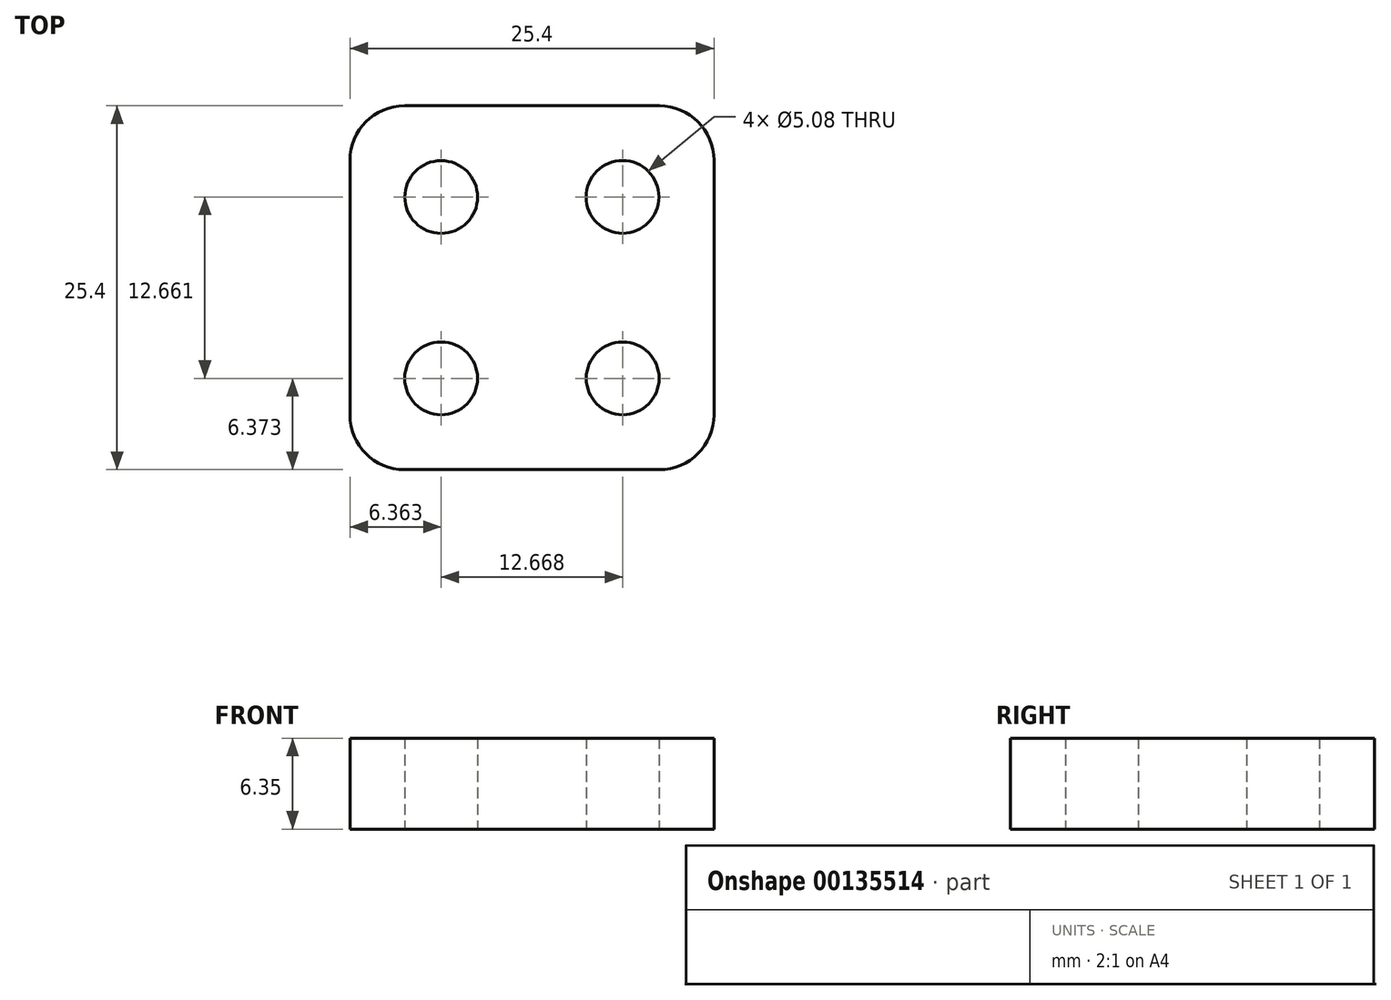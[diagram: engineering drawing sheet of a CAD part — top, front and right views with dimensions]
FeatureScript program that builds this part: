
annotation { "Feature Type Name" : "Feature", "Feature Type Description" : "" }
export const myFeature = defineFeature(function(context is Context, id is Id, definition is map)
    precondition{}
    {
        {
            var Q0;
            Q0=qCreatedBy(makeId("Top.planeOp"),FACE);
            var sketch = newSketch(context, id + "F0", { "sketchPlane" : qUnion([Q0])});
            skLineSegment(sketch, "E0.bottom", {"start": v(8.9, -12.7) * mm, "end": v(-8.9, -12.7) * mm});
            skLineSegment(sketch, "E0.top", {"start": v(8.9, 12.7) * mm, "end": v(-8.9, 12.7) * mm});
            skLineSegment(sketch, "E0.left", {"start": v(12.7, -8.9) * mm, "end": v(12.7, 8.9) * mm});
            skLineSegment(sketch, "E0.right", {"start": v(-12.7, -8.9) * mm, "end": v(-12.7, 8.9) * mm});
            skPoint(sketch, "E0.middle", {"position": v(0, 0) * mm});
            skPoint(sketch, "E1.visualSharp", {"position": v(-12.7, -12.7) * mm});
            skArc(sketch, "E1.filletArc", {"start": v(-12.7, -8.9) * mm, "mid": v(-11.58, -11.58) * mm, "end": v(-8.9, -12.7) * mm});
            skPoint(sketch, "E2.visualSharp", {"position": v(12.7, -12.7) * mm});
            skArc(sketch, "E2.filletArc", {"start": v(8.9, -12.7) * mm, "mid": v(11.58, -11.58) * mm, "end": v(12.7, -8.9) * mm});
            skPoint(sketch, "E3.visualSharp", {"position": v(-12.7, 12.7) * mm});
            skArc(sketch, "E3.filletArc", {"start": v(-8.9, 12.7) * mm, "mid": v(-11.58, 11.58) * mm, "end": v(-12.7, 8.9) * mm});
            skPoint(sketch, "E4.visualSharp", {"position": v(12.7, 12.7) * mm});
            skArc(sketch, "E4.filletArc", {"start": v(12.7, 8.9) * mm, "mid": v(11.58, 11.58) * mm, "end": v(8.9, 12.7) * mm});
            skSolve(sketch);
        }
        {
            var Q0;
            Q0 = qSketchRegion(id + "F0", true);
            extrude(context, id + "F1", {"entities" : qUnion([Q0]), "depth" : 6.35 * mm});
        }
        {
            var Q0;
            Q0=qCreatedBy(makeId("Top.planeOp"),FACE);
            var sketch = newSketch(context, id + "F2", { "sketchPlane" : qUnion([Q0])});
            skLineSegment(sketch, "E5", {"start": v(-12.67, 12.66) * mm, "end": v(12.66, -12.65) * mm, "construction": true});
            skLineSegment(sketch, "E6", {"start": v(12.66, 12.67) * mm, "end": v(-12.67, -12.66) * mm, "construction": true});
            skLineSegment(sketch, "E7", {"start": v(-12.67, 0) * mm, "end": v(0, -12.66) * mm, "construction": true});
            skLineSegment(sketch, "E8", {"start": v(0, -12.66) * mm, "end": v(12.66, 0) * mm, "construction": true});
            skLineSegment(sketch, "E9", {"start": v(12.66, 0) * mm, "end": v(0, 12.66) * mm, "construction": true});
            skLineSegment(sketch, "E10", {"start": v(0, 12.66) * mm, "end": v(-12.67, 0) * mm, "construction": true});
            skCircle(sketch, "E11", {"center": v(-6.34, -6.33) * mm, "radius": 2.54 * mm});
            skCircle(sketch, "E12", {"center": v(6.33, -6.33) * mm, "radius": 2.54 * mm});
            skCircle(sketch, "E13", {"center": v(6.32, 6.33) * mm, "radius": 2.54 * mm});
            skCircle(sketch, "E14", {"center": v(-6.33, 6.33) * mm, "radius": 2.54 * mm});
            skSolve(sketch);
        }
        {
            var Q0;
            Q0 = qSketchRegion(id + "F2", true);
            extrude(context, id + "F3", {"entities" : qUnion([Q0]), "operationType" : NewBodyOperationType.REMOVE, "depth" : 25.4 * mm, "hasSecondDirection" : true, "secondDirectionOppositeDirection" : true, "secondDirectionDepth" : 25.4 * mm});
        }
    });
